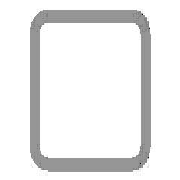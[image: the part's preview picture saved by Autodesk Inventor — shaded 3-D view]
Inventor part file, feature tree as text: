
AUTODESK INVENTOR PART (.ipt)
format: ipt  version: 2025.1 (Build 291241000, 241)  size: 133,632 bytes
history: native  units: mm (DEFAULTED — no unit token found)
features: other x4, sketch x2, extrude x1, plane x1
ambient origin geometry x8: Origin, YZ Plane, XZ Plane, XY Plane, X Axis, Y Axis, Z Axis, Center Point
bodies: Solid1 (feature_tree)
feature tree (8):
  parser-record x1  (decoder bookkeeping rows leaked as tree rows — omitted from the tree; the rows remain in map.json)
  other  "Driven Length"
  other  "Płaszczyzna początkowa"
  other  "Płaszczyzna końcowa"
  extrude  "Bryła"  TaperAngle=0.0deg  [1 undecoded]
  sketch  "Sketch3"  dims[d3=1500.0mm d4=0.0mm]
  plane  "Work Plane3"
  sketch  "Sketch4"  dims[d7=4.0mm d10=40.0mm d11=40.0mm d12=3.2mm d13=-0.0mm d14=1500.0mm d15=20.0mm d16=20.0mm d17=90.0deg d18=1500.0mm]
note: 1 required parameter value undecoded (feature->parameter linkage not recoverable at this tier; creation-order binding heuristic only, values carry confidence <= 0.55)
